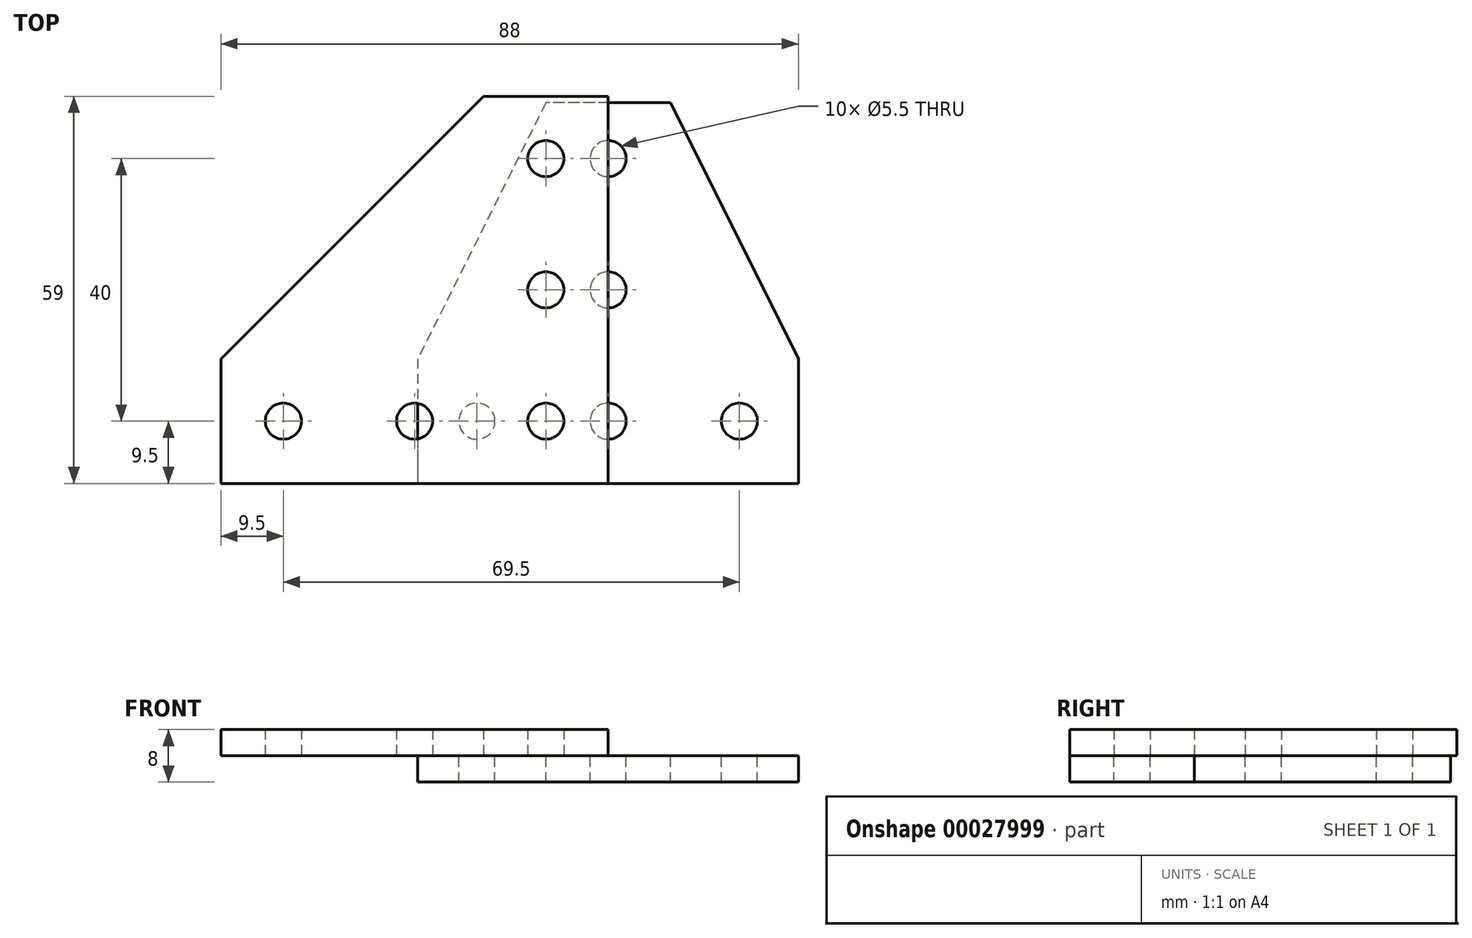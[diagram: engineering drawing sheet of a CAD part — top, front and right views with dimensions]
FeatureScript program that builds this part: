
annotation { "Feature Type Name" : "Feature", "Feature Type Description" : "" }
export const myFeature = defineFeature(function(context is Context, id is Id, definition is map)
    precondition{}
    {
        {
            var Q0;
            Q0=qCreatedBy(makeId("Top.planeOp"),FACE);
            var sketch = newSketch(context, id + "F0", { "sketchPlane" : qUnion([Q0])});
            skLineSegment(sketch, "E0", {"start": v(0, 0) * mm, "end": v(0, 59) * mm});
            skLineSegment(sketch, "E1", {"start": v(0, 59) * mm, "end": v(-19, 59) * mm});
            skLineSegment(sketch, "E2", {"start": v(-19, 59) * mm, "end": v(-59, 19) * mm});
            skLineSegment(sketch, "E3", {"start": v(-59, 19) * mm, "end": v(-59, 0) * mm});
            skLineSegment(sketch, "E4", {"start": v(-59, 0) * mm, "end": v(0, 0) * mm});
            skLineSegment(sketch, "E5", {"start": v(-9.5, 59) * mm, "end": v(-9.5, 0) * mm, "construction": true});
            skLineSegment(sketch, "E6", {"start": v(-59, 9.5) * mm, "end": v(0, 9.5) * mm, "construction": true});
            skCircle(sketch, "E7", {"center": v(-9.5, 9.5) * mm, "radius": 2.75 * mm});
            skCircle(sketch, "E8", {"center": v(-29.5, 9.5) * mm, "radius": 2.75 * mm});
            skCircle(sketch, "E9", {"center": v(-49.5, 9.5) * mm, "radius": 2.75 * mm});
            skLineSegment(sketch, "E10", {"start": v(0, 0) * mm, "end": v(-39, 39) * mm, "construction": true});
            skCircle(sketch, "E11.MirrorC", {"center": v(-9.5, 29.5) * mm, "radius": 2.75 * mm});
            skCircle(sketch, "E12.MirrorC", {"center": v(-9.5, 49.5) * mm, "radius": 2.75 * mm});
            skSolve(sketch);
        }
        {
            var Q0;
            Q0 = qSketchRegion(id + "F0", true);
            extrude(context, id + "F1", {"entities" : qUnion([Q0]), "depth" : 4 * mm});
        }
        {
            var Q0;
            Q0=qCreatedBy(makeId("Top.planeOp"),FACE);
            var sketch = newSketch(context, id + "F2", { "sketchPlane" : qUnion([Q0])});
            skLineSegment(sketch, "E13", {"start": v(-29, 0) * mm, "end": v(29, 0) * mm});
            skLineSegment(sketch, "E14", {"start": v(29, 0) * mm, "end": v(29, 19) * mm});
            skLineSegment(sketch, "E15", {"start": v(29, 19) * mm, "end": v(9.5, 58) * mm});
            skLineSegment(sketch, "E16", {"start": v(9.5, 58) * mm, "end": v(-9.5, 58) * mm});
            skLineSegment(sketch, "E17", {"start": v(-9.5, 58) * mm, "end": v(-29, 19) * mm});
            skLineSegment(sketch, "E18", {"start": v(-29, 19) * mm, "end": v(-29, 0) * mm});
            skLineSegment(sketch, "E19", {"start": v(-29, 9.5) * mm, "end": v(29, 9.5) * mm, "construction": true});
            skCircle(sketch, "E20", {"center": v(0, 9.5) * mm, "radius": 2.75 * mm});
            skCircle(sketch, "E21", {"center": v(-20, 9.5) * mm, "radius": 2.75 * mm});
            skCircle(sketch, "E22", {"center": v(20, 9.5) * mm, "radius": 2.75 * mm});
            skCircle(sketch, "E23", {"center": v(0, 29.5) * mm, "radius": 2.75 * mm});
            skCircle(sketch, "E24", {"center": v(0, 49.5) * mm, "radius": 2.75 * mm});
            skSolve(sketch);
        }
        {
            var Q0;
            Q0 = qSketchRegion(id + "F2", true);
            extrude(context, id + "F3", {"entities" : qUnion([Q0]), "oppositeDirection" : true, "depth" : 4 * mm});
        }
    });
